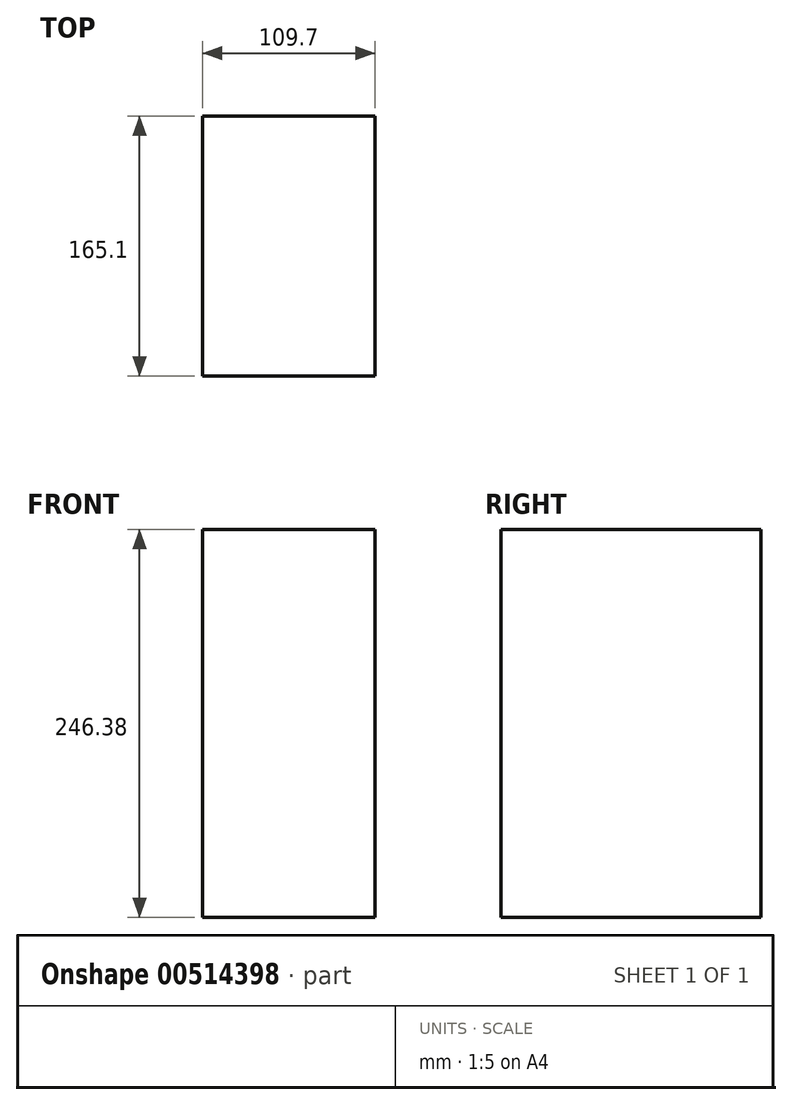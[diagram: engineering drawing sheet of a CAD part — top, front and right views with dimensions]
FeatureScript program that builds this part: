
annotation { "Feature Type Name" : "Feature", "Feature Type Description" : "" }
export const myFeature = defineFeature(function(context is Context, id is Id, definition is map)
    precondition{}
    {
        {
            var Q0;
            Q0=qCreatedBy(makeId("Top.planeOp"),FACE);
            var sketch = newSketch(context, id + "F0", { "sketchPlane" : qUnion([Q0])});
            skLineSegment(sketch, "E0.bottom", {"start": v(-54.85, 51.23) * mm, "end": v(54.85, 51.23) * mm});
            skLineSegment(sketch, "E0.top", {"start": v(-54.85, -51.23) * mm, "end": v(54.85, -51.23) * mm});
            skLineSegment(sketch, "E0.left", {"start": v(-54.85, 51.23) * mm, "end": v(-54.85, -51.23) * mm});
            skLineSegment(sketch, "E0.right", {"start": v(54.85, 51.23) * mm, "end": v(54.85, -51.23) * mm});
            skPoint(sketch, "E0.middle", {"position": v(0, 0) * mm});
            skSolve(sketch);
        }
        {
            var Q0;
            Q0=makeQuery(id+"F0.imprint","IMPRINT",FACE,{"disambiguationData":[TD([[makeQuery(id+"F0.imprint","IMPRINT",EDGE,{"derivedFrom":sQuery(id+"F0.wireOp",EDGE,"E0.bottom")}),-1.0]])]});
            extrude(context, id + "F1", {"entities" : qUnion([Q0]), "depth" : 246.38 * mm});
        }
        {
            var Q0;
            Q0=makeQuery(id+"F1.opExtrude","CAP_FACE",FACE,{"disambiguationData":[OSD([sQuery(id+"F0.wireOp",EDGE,"E0.bottom"),sQuery(id+"F0.wireOp",EDGE,"E0.top"),sQuery(id+"F0.wireOp",EDGE,"E0.left"),sQuery(id+"F0.wireOp",EDGE,"E0.right")])],"isStart":false});
            var sketch = newSketch(context, id + "F2", { "sketchPlane" : qUnion([Q0])});
            skLineSegment(sketch, "E1.bottom", {"start": v(-14.24, -51.23) * mm, "end": v(14.24, -51.23) * mm});
            skLineSegment(sketch, "E1.top", {"start": v(-14.24, 51.23) * mm, "end": v(14.24, 51.23) * mm});
            skLineSegment(sketch, "E1.left", {"start": v(-14.24, -51.23) * mm, "end": v(-14.24, 51.23) * mm});
            skLineSegment(sketch, "E1.right", {"start": v(14.24, -51.23) * mm, "end": v(14.24, 51.23) * mm});
            skPoint(sketch, "E1.middle", {"position": v(0, 0) * mm});
            skSolve(sketch);
        }
        {
            var Q0;
            Q0=makeQuery(id+"F1.opExtrude","SWEPT_FACE",FACE,{"disambiguationData":[OSD([sQuery(id+"F0.wireOp",EDGE,"E0.top")])]});
            extrude(context, id + "F3", {"entities" : qUnion([Q0]), "operationType" : NewBodyOperationType.ADD, "oppositeDirection" : true, "depth" : 165.1 * mm});
        }
    });
